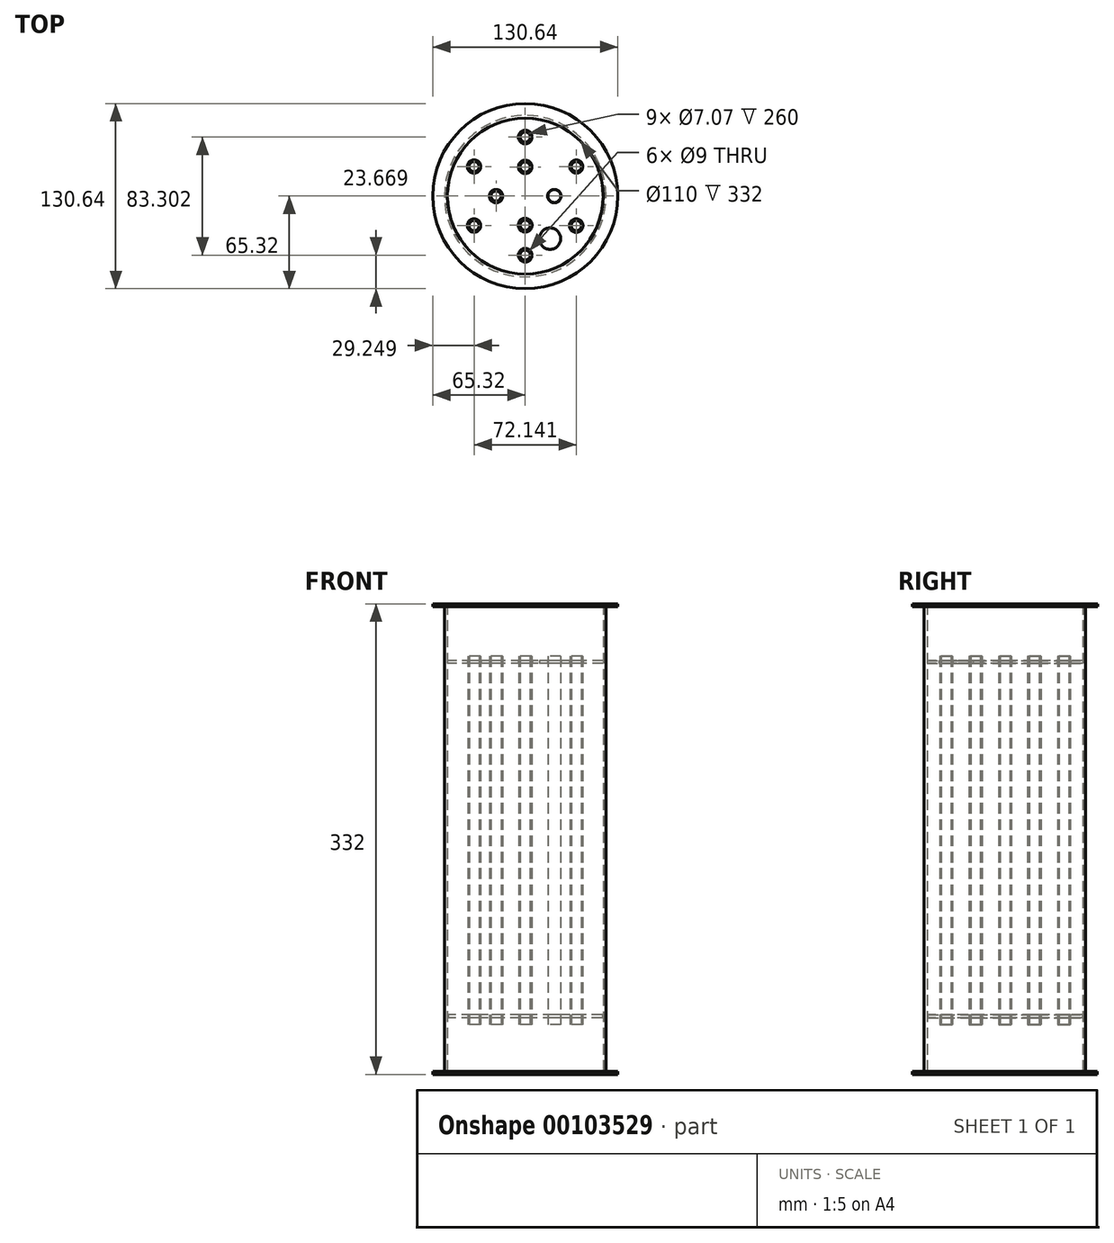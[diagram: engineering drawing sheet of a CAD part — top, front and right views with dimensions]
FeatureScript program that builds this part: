
annotation { "Feature Type Name" : "Feature", "Feature Type Description" : "" }
export const myFeature = defineFeature(function(context is Context, id is Id, definition is map)
    precondition{}
    {
        {
            var Q0;
            Q0=qCreatedBy(makeId("Top.planeOp"),FACE);
            var sketch = newSketch(context, id + "F0", { "sketchPlane" : qUnion([Q0])});
            skCircle(sketch, "E0", {"center": v(0, 0) * mm, "radius": 57 * mm});
            skCircle(sketch, "E1.0", {"center": v(0, 0) * mm, "radius": 55 * mm});
            skCircle(sketch, "E2", {"center": v(0, 0) * mm, "radius": 65.27 * mm});
            skSolve(sketch);
        }
        {
            var Q0;
            Q0=makeQuery(id+"F0.imprint","IMPRINT",FACE,{"disambiguationData":[TD([[makeQuery(id+"F0.imprint","IMPRINT",EDGE,{"derivedFrom":sQuery(id+"F0.wireOp",EDGE,"E0")}),1.0]])]});
            extrude(context, id + "F1", {"entities" : qUnion([Q0]), "depth" : 330 * mm});
        }
        {
            var Q0;
            Q0=qCreatedBy(makeId("Top.planeOp"),FACE);
            cPlane(context, id + "F2", {"entities" : qUnion([Q0]), "cplaneType" : CPlaneType.OFFSET, "offset" : 40 * mm, "width" : 150 * mm, "height" : 150 * mm});
        }
        {
            var Q0;
            Q0=qCreatedBy(id+"F2.planeOp",FACE);
            var sketch = newSketch(context, id + "F3", { "sketchPlane" : qUnion([Q0])});
            skCircle(sketch, "E3", {"center": v(0, 0) * mm, "radius": 54.5 * mm});
            skPoint(sketch, "E4", {"position": v(0, 41.65) * mm});
            skPoint(sketch, "E5.1.0", {"position": v(-36.07, 20.83) * mm});
            skPoint(sketch, "E5.2.0", {"position": v(-36.07, -20.83) * mm});
            skPoint(sketch, "E5.3.0", {"position": v(0, -41.65) * mm});
            skPoint(sketch, "E5.4.0", {"position": v(36.07, -20.83) * mm});
            skPoint(sketch, "E5.5.0", {"position": v(36.07, 20.83) * mm});
            skPoint(sketch, "E6", {"position": v(0, 20.56) * mm});
            skPoint(sketch, "E7.1.0", {"position": v(20.56, 0) * mm});
            skPoint(sketch, "E7.2.0", {"position": v(0, -20.56) * mm});
            skPoint(sketch, "E7.3.0", {"position": v(-20.56, 0) * mm});
            skCircle(sketch, "E8", {"center": v(0, 41.65) * mm, "radius": 4.5 * mm});
            skCircle(sketch, "E9", {"center": v(0, 41.65) * mm, "radius": 3.54 * mm});
            skCircle(sketch, "E10.1.0", {"center": v(-36.07, 20.83) * mm, "radius": 3.54 * mm});
            skCircle(sketch, "E10.1.2", {"center": v(-36.07, 20.83) * mm, "radius": 4.5 * mm});
            skCircle(sketch, "E10.2.0", {"center": v(-36.07, -20.83) * mm, "radius": 3.54 * mm});
            skCircle(sketch, "E10.2.2", {"center": v(-36.07, -20.83) * mm, "radius": 4.5 * mm});
            skCircle(sketch, "E10.3.0", {"center": v(0, -41.65) * mm, "radius": 3.54 * mm});
            skCircle(sketch, "E10.3.2", {"center": v(0, -41.65) * mm, "radius": 4.5 * mm});
            skCircle(sketch, "E10.4.0", {"center": v(36.07, -20.83) * mm, "radius": 3.54 * mm});
            skCircle(sketch, "E10.4.2", {"center": v(36.07, -20.83) * mm, "radius": 4.5 * mm});
            skCircle(sketch, "E10.5.0", {"center": v(36.07, 20.83) * mm, "radius": 3.54 * mm});
            skCircle(sketch, "E10.5.2", {"center": v(36.07, 20.83) * mm, "radius": 4.5 * mm});
            skCircle(sketch, "E11", {"center": v(0, 20.56) * mm, "radius": 4.54 * mm});
            skCircle(sketch, "E12", {"center": v(0, 20.56) * mm, "radius": 3.54 * mm});
            skCircle(sketch, "E13.1.1", {"center": v(-20.56, 0) * mm, "radius": 3.54 * mm});
            skCircle(sketch, "E13.1.2", {"center": v(-20.56, 0) * mm, "radius": 4.54 * mm});
            skCircle(sketch, "E13.2.1", {"center": v(0, -20.56) * mm, "radius": 3.54 * mm});
            skCircle(sketch, "E13.2.2", {"center": v(0, -20.56) * mm, "radius": 4.54 * mm});
            skCircle(sketch, "E13.3.1", {"center": v(20.56, 0) * mm, "radius": 3.54 * mm});
            skCircle(sketch, "E13.3.2", {"center": v(20.56, 0) * mm, "radius": 4.54 * mm});
            skSolve(sketch);
        }
        {
            var Q0;
            Q0 = qSketchRegion(id + "F3", true);
            extrude(context, id + "F4", {"entities" : qUnion([Q0]), "operationType" : NewBodyOperationType.ADD, "depth" : 2 * mm});
        }
        {
            var Q0;
            Q0=sQuery(id+"F3.wireOp",VERTEX,"E4");
            var Q1;
            Q1=sQuery(id+"F3.wireOp",VERTEX,"E6");
            var Q2;
            Q2=sQuery(id+"F3.wireOp",VERTEX,"E7.3.0");
            var Q3;
            Q3=sQuery(id+"F3.wireOp",VERTEX,"E5.1.0");
            var Q4;
            Q4=sQuery(id+"F3.wireOp",VERTEX,"E5.2.0");
            var Q5;
            Q5=sQuery(id+"F3.wireOp",VERTEX,"E7.2.0");
            var Q6;
            Q6=sQuery(id+"F3.wireOp",VERTEX,"E7.1.0");
            var Q7;
            Q7=sQuery(id+"F3.wireOp",VERTEX,"E5.5.0");
            var Q8;
            Q8=sQuery(id+"F3.wireOp",VERTEX,"E5.4.0");
            var Q9;
            Q9=sQuery(id+"F3.wireOp",VERTEX,"E5.3.0");
            var Q10;
            Q10=makeQuery(id+"F1.opExtrude","SWEPT_BODY",BODY,{"disambiguationData":[OSD([sQuery(id+"F0.wireOp",EDGE,"E0"),sQuery(id+"F0.wireOp",EDGE,"E1.0")])]});
            hole(context, id + "F5", {"style" : HoleStyle.SIMPLE, "endStyle" : HoleEndStyle.BLIND, "oppositeDirection" : true, "holeDiameter" : 10 * mm, "holeDepth" : 4 * mm, "locations" : qUnion([Q0, Q1, Q2, Q3, Q4, Q5, Q6, Q7, Q8, Q9]), "scope" : qUnion([Q10])});
        }
        {
            var Q0;
            Q0=qCreatedBy(makeId("Top.planeOp"),FACE);
            cPlane(context, id + "F6", {"entities" : qUnion([Q0]), "cplaneType" : CPlaneType.OFFSET, "offset" : 290 * mm, "width" : 150 * mm, "height" : 150 * mm});
        }
        {
            var Q0;
            Q0=qCreatedBy(id+"F6.planeOp",FACE);
            var sketch = newSketch(context, id + "F7", { "sketchPlane" : qUnion([Q0])});
            skCircle(sketch, "E14", {"center": v(0, 0) * mm, "radius": 55 * mm});
            skCircle(sketch, "E15", {"center": v(-36.1, 20.83) * mm, "radius": 4.73 * mm});
            skCircle(sketch, "E16", {"center": v(0, 20.6) * mm, "radius": 4.77 * mm});
            skCircle(sketch, "E17", {"center": v(0, 41.66) * mm, "radius": 4.82 * mm});
            skCircle(sketch, "E18", {"center": v(36.06, 20.85) * mm, "radius": 4.66 * mm});
            skCircle(sketch, "E19", {"center": v(-20.6, 0) * mm, "radius": 4.7 * mm});
            skCircle(sketch, "E20", {"center": v(20.58, 0) * mm, "radius": 4.74 * mm});
            skCircle(sketch, "E21", {"center": v(-36.1, -20.79) * mm, "radius": 4.72 * mm});
            skCircle(sketch, "E22", {"center": v(0, -20.55) * mm, "radius": 4.9 * mm});
            skCircle(sketch, "E23", {"center": v(0, -41.72) * mm, "radius": 4.84 * mm});
            skCircle(sketch, "E24", {"center": v(36, -20.85) * mm, "radius": 4.8 * mm});
            skPoint(sketch, "E25", {"position": v(17.51, -30.03) * mm});
            skCircle(sketch, "E26", {"center": v(17.51, -30.03) * mm, "radius": 7.56 * mm});
            skSolve(sketch);
        }
        {
            var Q0;
            Q0=makeQuery(id+"F7.imprint","IMPRINT",FACE,{"disambiguationData":[TD([[makeQuery(id+"F7.imprint","IMPRINT",EDGE,{"derivedFrom":sQuery(id+"F7.wireOp",EDGE,"E14")}),1.0]])]});
            extrude(context, id + "F8", {"entities" : qUnion([Q0]), "depth" : 2 * mm});
        }
        {
            var Q0;
            Q0=makeQuery(id+"F1.opExtrude","CAP_FACE",FACE,{"disambiguationData":[OSD([sQuery(id+"F0.wireOp",EDGE,"E0"),sQuery(id+"F0.wireOp",EDGE,"E1.0")])],"isStart":false});
            var sketch = newSketch(context, id + "F9", { "sketchPlane" : qUnion([Q0])});
            skCircle(sketch, "E27", {"center": v(0, 0) * mm, "radius": 65.32 * mm});
            skSolve(sketch);
        }
        {
            var Q0;
            Q0=makeQuery(id+"F9.imprint","IMPRINT",FACE,{"disambiguationData":[TD([[makeQuery(id+"F9.imprint","IMPRINT",EDGE,{"derivedFrom":sQuery(id+"F9.wireOp",EDGE,"E27")}),1.0]])]});
            var Q1;
            Q1=makeQuery(id+"F9.imprint","IMPRINT",FACE,{"disambiguationData":[TD([[makeQuery(id+"F9.imprint","IMPRINT",EDGE,{"derivedFrom":makeQuery(id+"F1.opExtrude","CAP_EDGE",EDGE,{"disambiguationData":[OSD([sQuery(id+"F0.wireOp",EDGE,"E0")])],"isStart":false})}),1.0]])]});
            extrude(context, id + "F10", {"entities" : qUnion([Q0, Q1]), "operationType" : NewBodyOperationType.ADD, "depth" : 2 * mm});
        }
        {
            var Q0;
            Q0=makeQuery(id+"F0.imprint","IMPRINT",FACE,{"disambiguationData":[TD([[makeQuery(id+"F0.imprint","IMPRINT",EDGE,{"derivedFrom":sQuery(id+"F0.wireOp",EDGE,"E0")}),-1.0]])]});
            extrude(context, id + "F11", {"entities" : qUnion([Q0]), "operationType" : NewBodyOperationType.ADD, "depth" : 2 * mm});
        }
        {
            var Q0;
            Q0=makeQuery(id+"F3.imprint","IMPRINT",FACE,{"disambiguationData":[TD([[makeQuery(id+"F3.imprint","IMPRINT",EDGE,{"derivedFrom":sQuery(id+"F3.wireOp",EDGE,"E10.2.0")}),-1.0]])]});
            var Q1;
            Q1=makeQuery(id+"F3.imprint","IMPRINT",FACE,{"disambiguationData":[TD([[makeQuery(id+"F3.imprint","IMPRINT",EDGE,{"derivedFrom":sQuery(id+"F3.wireOp",EDGE,"E13.1.1")}),-1.0]])]});
            var Q2;
            Q2=makeQuery(id+"F3.imprint","IMPRINT",FACE,{"disambiguationData":[TD([[makeQuery(id+"F3.imprint","IMPRINT",EDGE,{"derivedFrom":sQuery(id+"F3.wireOp",EDGE,"E10.3.0")}),-1.0]])]});
            var Q3;
            Q3=makeQuery(id+"F3.imprint","IMPRINT",FACE,{"disambiguationData":[TD([[makeQuery(id+"F3.imprint","IMPRINT",EDGE,{"derivedFrom":sQuery(id+"F3.wireOp",EDGE,"E10.4.0")}),-1.0]])]});
            var Q4;
            Q4=makeQuery(id+"F3.imprint","IMPRINT",FACE,{"disambiguationData":[TD([[makeQuery(id+"F3.imprint","IMPRINT",EDGE,{"derivedFrom":sQuery(id+"F3.wireOp",EDGE,"E13.2.1")}),-1.0]])]});
            var Q5;
            Q5=makeQuery(id+"F3.imprint","IMPRINT",FACE,{"disambiguationData":[TD([[makeQuery(id+"F3.imprint","IMPRINT",EDGE,{"derivedFrom":sQuery(id+"F3.wireOp",EDGE,"E10.5.0")}),-1.0]])]});
            var Q6;
            Q6=makeQuery(id+"F3.imprint","IMPRINT",FACE,{"disambiguationData":[TD([[makeQuery(id+"F3.imprint","IMPRINT",EDGE,{"derivedFrom":sQuery(id+"F3.wireOp",EDGE,"E8")}),1.0]])]});
            var Q7;
            Q7=makeQuery(id+"F3.imprint","IMPRINT",FACE,{"disambiguationData":[TD([[makeQuery(id+"F3.imprint","IMPRINT",EDGE,{"derivedFrom":sQuery(id+"F3.wireOp",EDGE,"E11")}),1.0]])]});
            var Q8;
            Q8=makeQuery(id+"F3.imprint","IMPRINT",FACE,{"disambiguationData":[TD([[makeQuery(id+"F3.imprint","IMPRINT",EDGE,{"derivedFrom":sQuery(id+"F3.wireOp",EDGE,"E10.1.0")}),-1.0]])]});
            var Q9;
            Q9=makeQuery(id+"F3.imprint","IMPRINT",FACE,{"disambiguationData":[TD([[makeQuery(id+"F3.imprint","IMPRINT",EDGE,{"derivedFrom":sQuery(id+"F3.wireOp",EDGE,"E13.3.1")}),1.0]])]});
            var Q10;
            Q10=makeQuery(id+"F3.imprint","IMPRINT",FACE,{"disambiguationData":[TD([[makeQuery(id+"F3.imprint","IMPRINT",EDGE,{"derivedFrom":sQuery(id+"F3.wireOp",EDGE,"E13.3.1")}),-1.0]])]});
            extrude(context, id + "F12", {"entities" : qUnion([Q0, Q1, Q2, Q3, Q4, Q5, Q6, Q7, Q8, Q9, Q10]), "depth" : 255 * mm, "hasSecondDirection" : true, "secondDirectionOppositeDirection" : true, "secondDirectionDepth" : 5 * mm});
        }
    });
